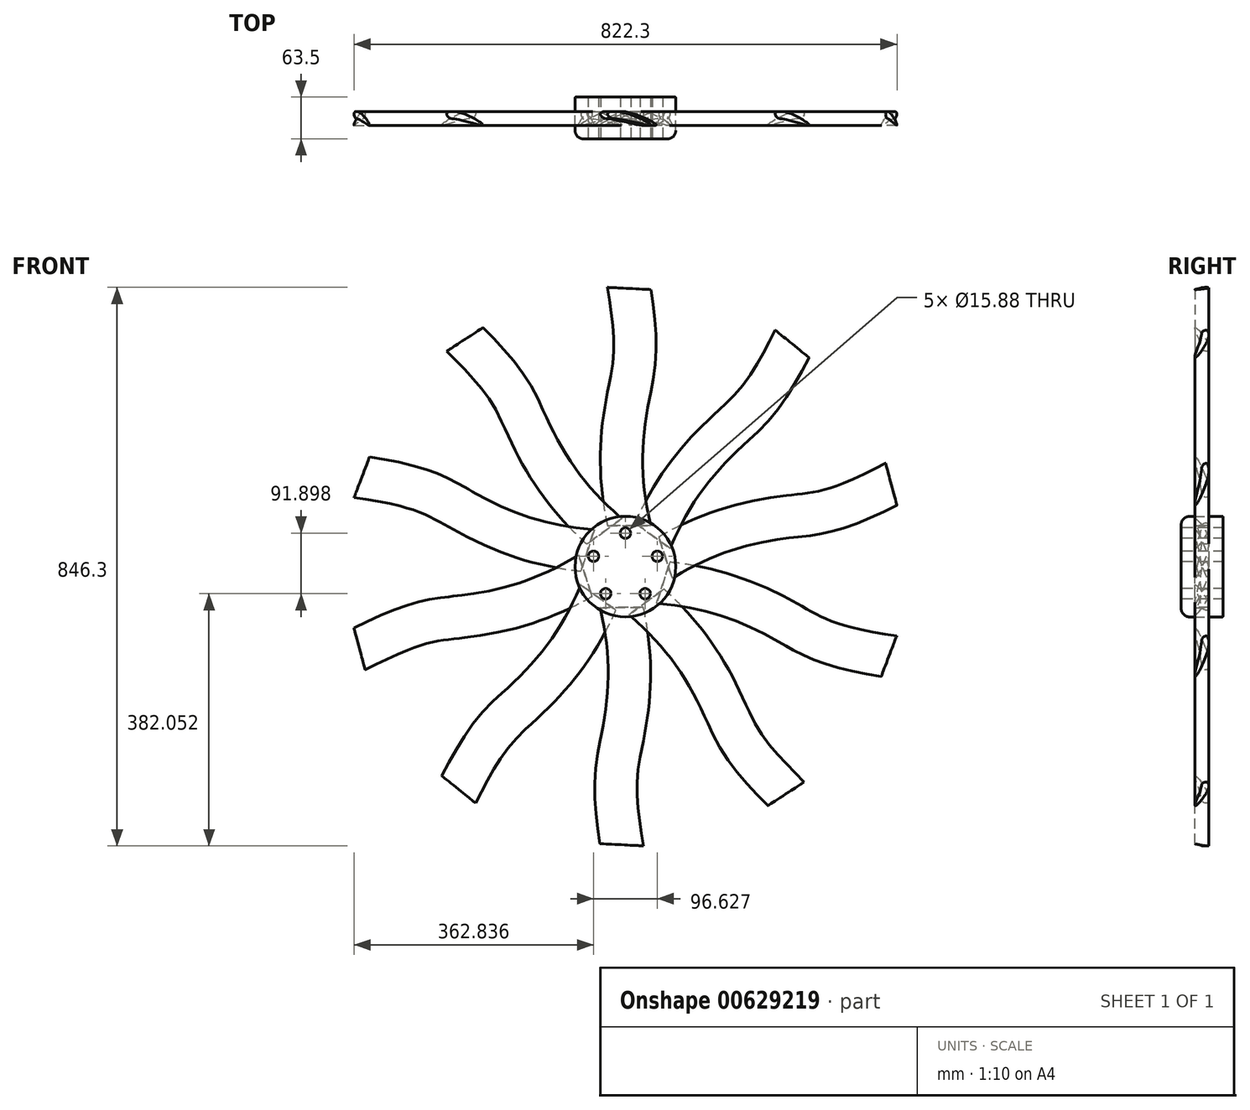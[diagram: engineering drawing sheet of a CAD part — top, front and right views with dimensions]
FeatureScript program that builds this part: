
annotation { "Feature Type Name" : "Feature", "Feature Type Description" : "" }
export const myFeature = defineFeature(function(context is Context, id is Id, definition is map)
    precondition{}
    {
        {
            var Q0;
            Q0=qCreatedBy(makeId("Top.planeOp"),FACE);
            var sketch = newSketch(context, id + "F0", { "sketchPlane" : qUnion([Q0])});
            skLineSegment(sketch, "E0.bottom", {"start": v(0, 31.75) * mm, "end": v(74.61, 31.75) * mm});
            skLineSegment(sketch, "E0.top", {"start": v(0, -31.75) * mm, "end": v(63.5, -31.75) * mm});
            skLineSegment(sketch, "E0.left", {"start": v(0, 31.75) * mm, "end": v(0, -31.75) * mm});
            skLineSegment(sketch, "E0.right", {"start": v(76.2, 30.16) * mm, "end": v(76.2, -19.05) * mm});
            skPoint(sketch, "E0.middle", {"position": v(38.1, 0) * mm});
            skPoint(sketch, "E1.visualSharp", {"position": v(76.2, -31.75) * mm});
            skArc(sketch, "E1.filletArc", {"start": v(63.5, -31.75) * mm, "mid": v(72.48, -28.03) * mm, "end": v(76.2, -19.05) * mm});
            skPoint(sketch, "E2.visualSharp", {"position": v(76.2, 31.75) * mm});
            skArc(sketch, "E2.filletArc", {"start": v(76.2, 30.16) * mm, "mid": v(75.74, 31.29) * mm, "end": v(74.61, 31.75) * mm});
            skLineSegment(sketch, "E3.filletArc", {"start": v(200.4, 35.53) * mm, "end": v(200.4, 35.53) * mm});
            skLineSegment(sketch, "E4.bottom", {"start": v(146.92, -13.37) * mm, "end": v(154.06, -13.37) * mm});
            skLineSegment(sketch, "E4.top", {"start": v(146.92, 13.37) * mm, "end": v(154.06, 13.37) * mm});
            skLineSegment(sketch, "E4.left", {"start": v(146.92, -13.37) * mm, "end": v(146.92, 13.37) * mm});
            skLineSegment(sketch, "E4.right", {"start": v(154.06, -13.37) * mm, "end": v(154.06, 13.37) * mm});
            skPoint(sketch, "E4.middle", {"position": v(150.49, 0) * mm});
            skSolve(sketch);
        }
        {
            var Q0;
            Q0=makeQuery(id+"F0.imprint","IMPRINT",FACE,{"disambiguationData":[TD([[makeQuery(id+"F0.imprint","IMPRINT",EDGE,{"derivedFrom":sQuery(id+"F0.wireOp",EDGE,"LdIDLeoo-MP7i-XAHj-biJ0-kHLxu66d2bUH")}),1.0]])]});
            var Q1;
            Q1=makeQuery(id+"F0.imprint","IMPRINT",FACE,{"disambiguationData":[TD([[makeQuery(id+"F0.imprint","IMPRINT",EDGE,{"derivedFrom":sQuery(id+"F0.wireOp",EDGE,"E0.bottom")}),-1.0]])]});
            var Q2;
            Q2=sQuery(id+"F0.wireOp",EDGE,"E0.left");
            revolve(context, id + "F1", {"entities" : qUnion([Q0, Q1]), "axis" : qUnion([Q2]), "revolveType" : RevolveType.FULL});
        }
        {
            var Q0;
            Q0=makeQuery(id+"F1.opRevolve","SWEPT_FACE",FACE,{"disambiguationData":[OSD([sQuery(id+"F0.wireOp",EDGE,"E0.top")])]});
            var sketch = newSketch(context, id + "F2", { "sketchPlane" : qUnion([Q0])});
            skCircle(sketch, "E5", {"center": v(0, 50.8) * mm, "radius": 7.94 * mm});
            skCircle(sketch, "E6.1.0", {"center": v(-48.31, 15.7) * mm, "radius": 7.94 * mm});
            skCircle(sketch, "E6.2.0", {"center": v(-29.86, -41.1) * mm, "radius": 7.94 * mm});
            skCircle(sketch, "E6.3.0", {"center": v(29.86, -41.1) * mm, "radius": 7.94 * mm});
            skCircle(sketch, "E6.4.0", {"center": v(48.31, 15.7) * mm, "radius": 7.94 * mm});
            skPoint(sketch, "E6.center", {"position": v(0, 0) * mm});
            skSolve(sketch);
        }
        {
            var Q0;
            Q0=makeQuery(id+"F2.imprint","IMPRINT",FACE,{"disambiguationData":[TD([[makeQuery(id+"F2.imprint","IMPRINT",EDGE,{"derivedFrom":sQuery(id+"F2.wireOp",EDGE,"E6.1.0")}),1.0]])]});
            var Q1;
            Q1=makeQuery(id+"F2.imprint","IMPRINT",FACE,{"disambiguationData":[TD([[makeQuery(id+"F2.imprint","IMPRINT",EDGE,{"derivedFrom":sQuery(id+"F2.wireOp",EDGE,"E5")}),1.0]])]});
            var Q2;
            Q2=makeQuery(id+"F2.imprint","IMPRINT",FACE,{"disambiguationData":[TD([[makeQuery(id+"F2.imprint","IMPRINT",EDGE,{"derivedFrom":sQuery(id+"F2.wireOp",EDGE,"E6.4.0")}),1.0]])]});
            var Q3;
            Q3=makeQuery(id+"F2.imprint","IMPRINT",FACE,{"disambiguationData":[TD([[makeQuery(id+"F2.imprint","IMPRINT",EDGE,{"derivedFrom":sQuery(id+"F2.wireOp",EDGE,"E6.3.0")}),1.0]])]});
            var Q4;
            Q4=makeQuery(id+"F2.imprint","IMPRINT",FACE,{"disambiguationData":[TD([[makeQuery(id+"F2.imprint","IMPRINT",EDGE,{"derivedFrom":sQuery(id+"F2.wireOp",EDGE,"E6.2.0")}),1.0]])]});
            extrude(context, id + "F3", {"entities" : qUnion([Q0, Q1, Q2, Q3, Q4]), "operationType" : NewBodyOperationType.REMOVE, "endBound" : BoundingType.THROUGH_ALL, "oppositeDirection" : true, "depth" : 25.4 * mm, "offsetDistance" : 25.4 * mm, "hasSecondDirection" : true, "secondDirectionOppositeDirection" : false, "secondDirectionDepth" : 25.4 * mm});
        }
        {
            var Q0;
            Q0=qCreatedBy(makeId("Top.planeOp"),FACE);
            cPlane(context, id + "F4", {"entities" : qUnion([Q0]), "cplaneType" : CPlaneType.OFFSET, "offset" : 63.5 * mm, "width" : 152.4 * mm, "height" : 152.4 * mm});
        }
        {
            var Q0;
            Q0=qCreatedBy(id+"F4.planeOp",FACE);
            var sketch = newSketch(context, id + "F5", { "sketchPlane" : qUnion([Q0])});
            skFitSpline(sketch, "E7", {"points": [v(38.16, -10.71) * mm, v(0, 7.34) * mm, v(-25.25, 8.59) * mm, v(-27.6, 6.22) * mm, v(-24.52, 1.1) * mm, v(-4.65, -2.7) * mm, v(38.16, -10.71) * mm]});
            skSolve(sketch);
        }
        {
            var Q0;
            Q0=qCreatedBy(makeId("Front.planeOp"),FACE);
            var sketch = newSketch(context, id + "F6", { "sketchPlane" : qUnion([Q0])});
            skFitSpline(sketch, "E8", {"points": [v(0, 61.98) * mm, v(0, 264.32) * mm, v(0, 421.76) * mm], "startDerivative": vector(-113.77, 506.48) * mm, "endDerivative": vector(-97.09, 575.9) * mm});
            skSolve(sketch);
        }
        {
            var Q0;
            Q0 = qSketchRegion(id + "F5", true);
            var Q1;
            Q1 = qConstructionFilter(qBodyType(qCreatedBy(id + "F6" ,EDGE), BodyType.WIRE), ConstructionObject.NO);
            sweep(context, id + "F7", {"profiles" : qUnion([Q0]), "path" : qUnion([Q1])});
        }
        {
            var Q0;
            Q0=makeQuery(id+"F7.opSweep","SWEPT_BODY",BODY,{"disambiguationData":[OSD([sQuery(id+"F5.wireOp",EDGE,"E7"),sQuery(id+"F6.wireOp",EDGE,"E8")])]});
            var Q1;
            Q1=sQuery(id+"F0.wireOp",EDGE,"E0.left");
            circularPattern(context, id + "F8", {"entities" : qUnion([Q0]), "axis" : qUnion([Q1]), "angle" : 360 * degree, "instanceCount" : 10, "equalSpace" : true});
        }
    });
